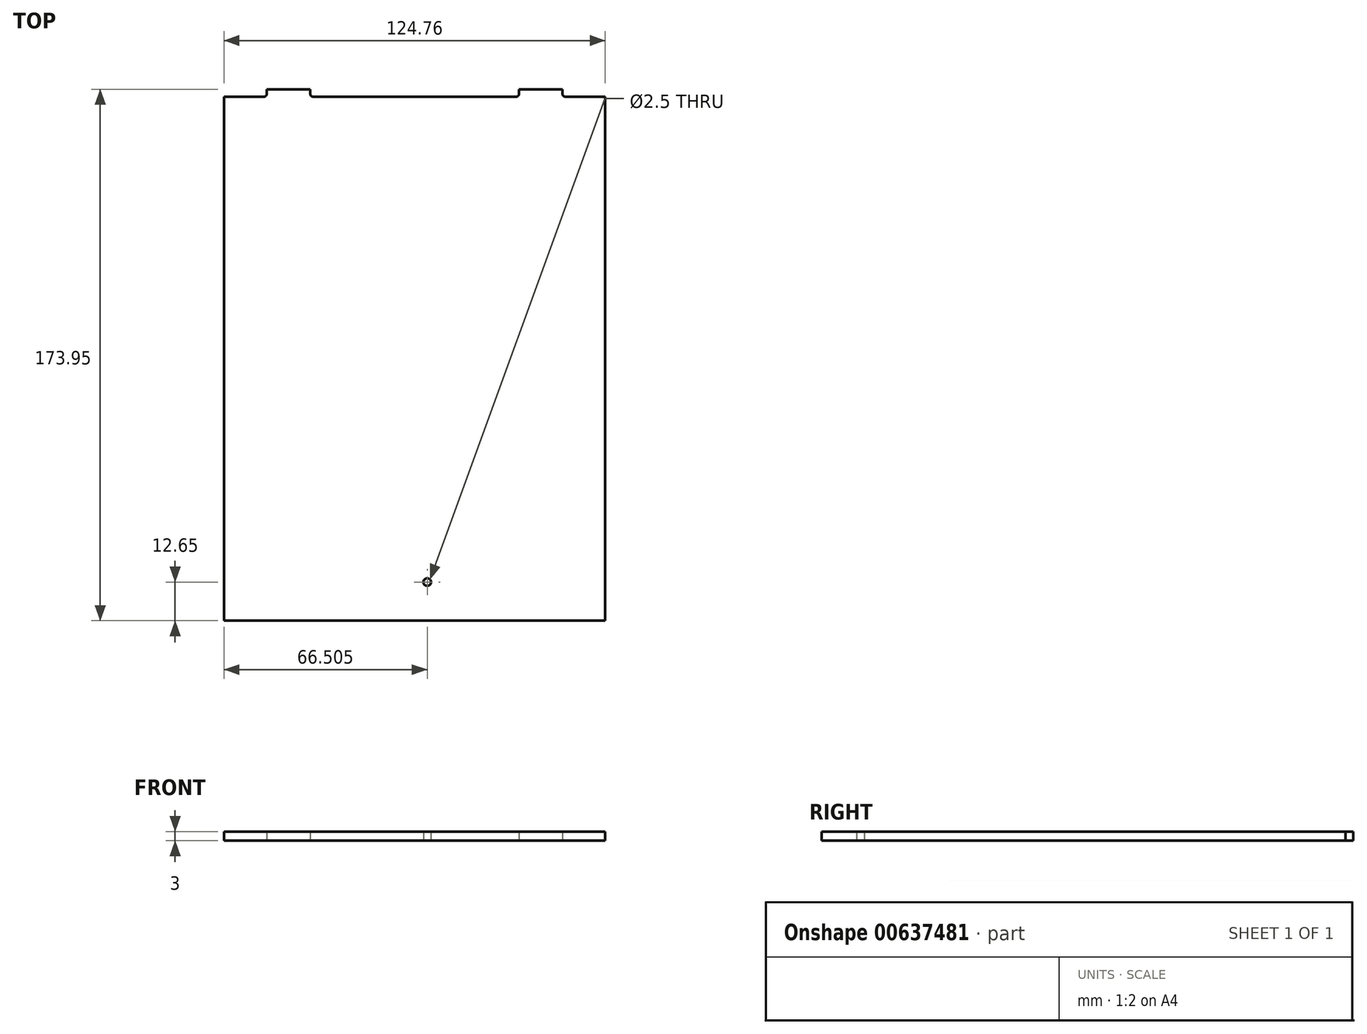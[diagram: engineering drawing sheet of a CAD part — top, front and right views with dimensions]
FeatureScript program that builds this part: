
annotation { "Feature Type Name" : "Feature", "Feature Type Description" : "" }
export const myFeature = defineFeature(function(context is Context, id is Id, definition is map)
    precondition{}
    {
        {
            var Q0;
            Q0=qCreatedBy(makeId("Top.planeOp"),FACE);
            var sketch = newSketch(context, id + "F0", { "sketchPlane" : qUnion([Q0])});
            skLineSegment(sketch, "E0.bottom", {"start": v(62.38, 85.75) * mm, "end": v(-62.37, 85.75) * mm});
            skLineSegment(sketch, "E0.top", {"start": v(62.37, -85.75) * mm, "end": v(-62.38, -85.75) * mm});
            skLineSegment(sketch, "E0.left", {"start": v(62.38, 85.75) * mm, "end": v(62.37, -85.75) * mm});
            skLineSegment(sketch, "E0.right", {"start": v(-62.37, 85.75) * mm, "end": v(-62.38, -85.75) * mm});
            skPoint(sketch, "E0.middle", {"position": v(0, 0) * mm});
            skLineSegment(sketch, "E1.bottom", {"start": v(-48.37, 85.75) * mm, "end": v(-34.17, 85.75) * mm});
            skLineSegment(sketch, "E1.top", {"start": v(-48.37, 88.2) * mm, "end": v(-34.17, 88.2) * mm});
            skLineSegment(sketch, "E1.left", {"start": v(-48.37, 85.75) * mm, "end": v(-48.37, 88.2) * mm});
            skLineSegment(sketch, "E1.right", {"start": v(-34.18, 85.75) * mm, "end": v(-34.18, 88.2) * mm});
            skCircle(sketch, "E2", {"center": v(4.12, -73.1) * mm, "radius": 1.25 * mm});
            skLineSegment(sketch, "E3.MirrorCS", {"start": v(34.18, 85.75) * mm, "end": v(34.18, 88.2) * mm});
            skLineSegment(sketch, "E4.MirrorCS", {"start": v(48.37, 85.75) * mm, "end": v(34.17, 85.75) * mm});
            skLineSegment(sketch, "E5.MirrorCS", {"start": v(48.37, 88.2) * mm, "end": v(34.17, 88.2) * mm});
            skLineSegment(sketch, "E6.MirrorCS", {"start": v(48.38, 85.75) * mm, "end": v(48.38, 88.2) * mm});
            skSolve(sketch);
        }
        {
            var Q0;
            Q0 = qSketchRegion(id + "F0", true);
            var Q1;
            Q1=makeQuery(id+"F0.imprint","IMPRINT",FACE,{"disambiguationData":[TD([[makeQuery(id+"F0.imprint","IMPRINT",EDGE,{"derivedFrom":sQuery(id+"F0.wireOp",EDGE,"E0.top")}),-1.0]])]});
            extrude(context, id + "F1", {"entities" : qUnion([Q0, Q1]), "depth" : 3 * mm, "offsetDistance" : 25 * mm});
        }
        {
            var Q0;
            Q0=makeQuery(id+"F1.opExtrude","SWEPT_EDGE",EDGE,{"disambiguationData":[OSD([sQuery(id+"F0.wireOp",EDGE,"E0.bottom"),sQuery(id+"F0.wireOp",EDGE,"E1.bottom"),sQuery(id+"F0.wireOp",EDGE,"E1.left")])]});
            var Q1;
            Q1=makeQuery(id+"F1.opExtrude","SWEPT_EDGE",EDGE,{"disambiguationData":[OSD([sQuery(id+"F0.wireOp",EDGE,"E0.bottom"),sQuery(id+"F0.wireOp",EDGE,"E1.bottom"),sQuery(id+"F0.wireOp",EDGE,"E1.right")])]});
            var Q2;
            Q2=makeQuery(id+"F1.opExtrude","SWEPT_EDGE",EDGE,{"disambiguationData":[OSD([sQuery(id+"F0.wireOp",EDGE,"E0.bottom"),sQuery(id+"F0.wireOp",EDGE,"E4.MirrorCS"),sQuery(id+"F0.wireOp",EDGE,"E6.MirrorCS")])]});
            var Q3;
            Q3=makeQuery(id+"F1.opExtrude","SWEPT_EDGE",EDGE,{"disambiguationData":[OSD([sQuery(id+"F0.wireOp",EDGE,"E0.bottom"),sQuery(id+"F0.wireOp",EDGE,"E3.MirrorCS"),sQuery(id+"F0.wireOp",EDGE,"E4.MirrorCS")])]});
            fillet(context, id + "F2", {"entities" : qUnion([Q0, Q1, Q2, Q3]), "radius" : 1 * mm, "tangentPropagation" : true, "allowEdgeOverflow" : false});
        }
    });
